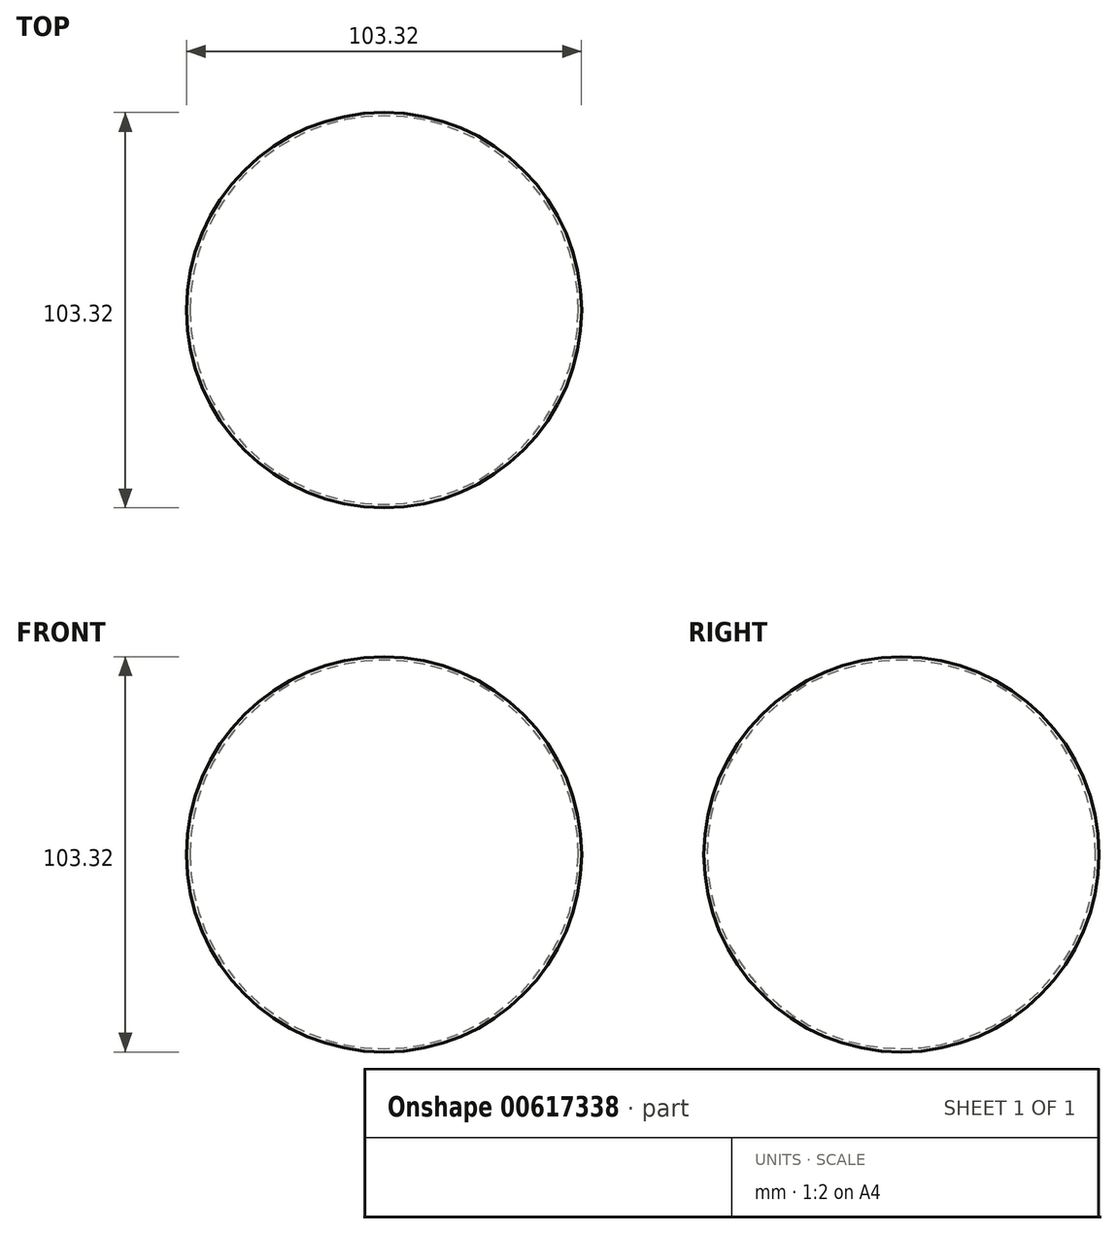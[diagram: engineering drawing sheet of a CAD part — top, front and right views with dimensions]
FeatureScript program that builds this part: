
annotation { "Feature Type Name" : "Feature", "Feature Type Description" : "" }
export const myFeature = defineFeature(function(context is Context, id is Id, definition is map)
    precondition{}
    {
        {
            var Q0;
            Q0=qCreatedBy(makeId("Top.planeOp"),FACE);
            var sketch = newSketch(context, id + "F0", { "sketchPlane" : qUnion([Q0])});
            skCircle(sketch, "E0", {"center": v(0, 0) * mm, "radius": 51.66 * mm});
            skCircle(sketch, "E1", {"center": v(0, 0) * mm, "radius": 50.8 * mm});
            skSolve(sketch);
        }
        {
            var Q0;
            Q0=qCreatedBy(makeId("Right.planeOp"),FACE);
            var sketch = newSketch(context, id + "F1", { "sketchPlane" : qUnion([Q0])});
            skCircle(sketch, "E2", {"center": v(0, 0) * mm, "radius": 50.8 * mm});
            skSolve(sketch);
        }
        {
            var Q0;
            Q0=makeQuery(id+"F0.imprint","IMPRINT",FACE,{"disambiguationData":[TD([[makeQuery(id+"F0.imprint","IMPRINT",EDGE,{"derivedFrom":sQuery(id+"F0.wireOp",EDGE,"E0")}),1.0]])]});
            var Q1;
            Q1=sQuery(id+"F1.wireOp",EDGE,"E2");
            sweep(context, id + "F2", {"profiles" : qUnion([Q0]), "path" : qUnion([Q1])});
        }
    });
